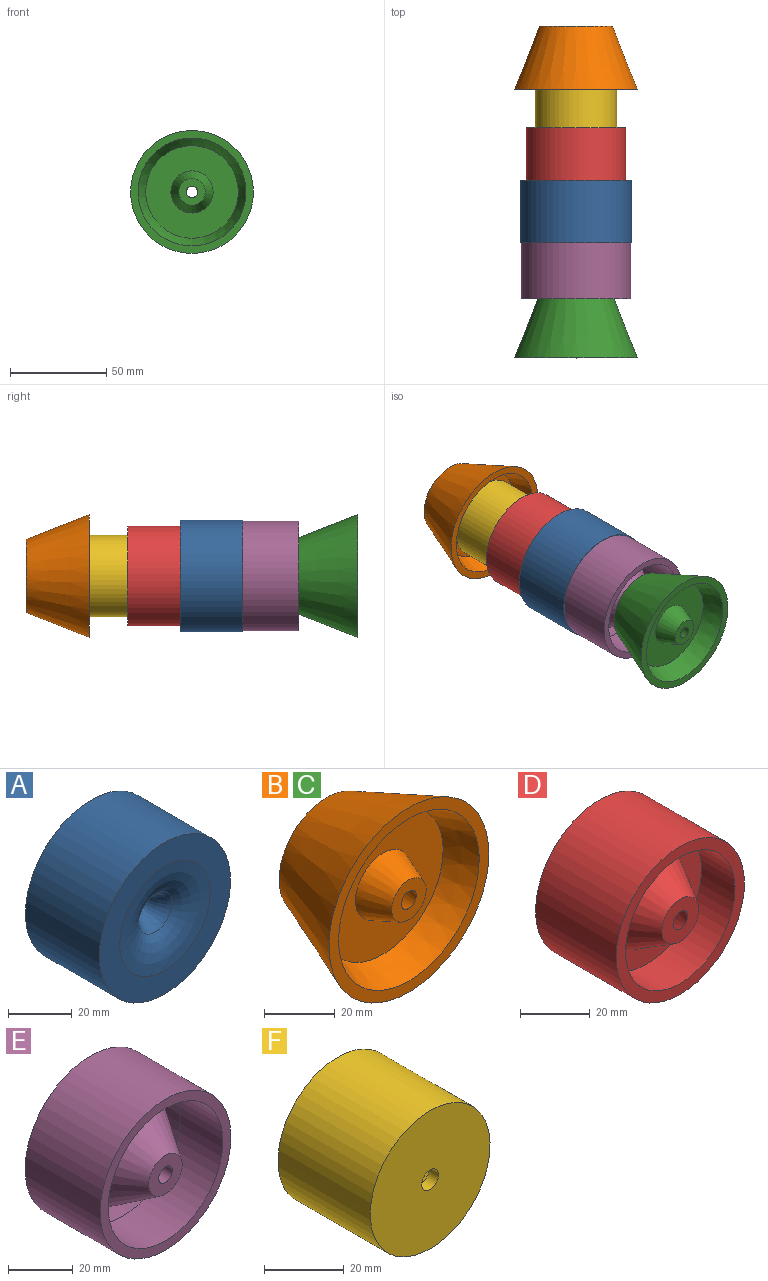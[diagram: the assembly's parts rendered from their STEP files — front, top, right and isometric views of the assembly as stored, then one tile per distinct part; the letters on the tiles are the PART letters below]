
ASSEMBLY  parts=6 mates=5
PART A: 14 faces, bbox 58.2x32.7x58.2 mm
  f0: revolved ~14.74x14.74mm, area 368.1mm2, adj f1,f6
  f1: revolved ~14.4x14.4mm, area 348.3mm2, adj f0,f2
  f2: revolved ~38.13x38.13mm, area 1043mm2, adj f1,f3
  f3: plane 58.18x58.18mm, normal (0,1,0), area 1516.7mm2, adj f2,f4
  f4: cylinder r=29.09mm len=58.18mm, axis (0,-1,0), area 5980.6mm2, adj f3,f5
  f5: plane 58.18x58.18mm, normal (0,-1,0), area 1398.9mm2, adj f4,f6
  f6: revolved ~40.05x40.05mm, area 1153.7mm2, adj f0,f5
  f7: revolved ~20.42x20.42mm, area 522.9mm2, adj f8,f13
  f8: revolved ~20.85x20.85mm, area 544.5mm2, adj f7,f9
  f9: revolved ~41.31x41.31mm, area 1061.5mm2, adj f8,f10
  f10: plane 50.57x50.57mm, normal (0,1,0), area 668.7mm2, adj f9,f11
  f11: cylinder r=25.29mm len=50.57mm, axis (0,-1,0), area 4153.1mm2, adj f10,f12
  f12: plane 50.57x50.57mm, normal (0,-1,0), area 782.4mm2, adj f11,f13
  f13: revolved ~39.52x39.52mm, area 960mm2, adj f7,f12
PART B: 13 faces, bbox 64x32.9x64 mm
  f0: cone r=6.91mm half-angle=21.4deg, axis (0,1,0), area 628.3mm2, adj f1,f7
  f1: plane 13.82x13.82mm, normal (0,-1,0), area 122.3mm2, adj f0,f2
  f2: cone r=15.84mm half-angle=21.4deg, axis (0,1,0), area 2085.6mm2, adj f1,f3
  f3: plane 38.08x38.08mm, normal (0,1,0), area 350.8mm2, adj f2,f4
  f4: cone r=31.98mm half-angle=21.5deg, axis (0,-1,0), area 5659.5mm2, adj f3,f5
  f5: plane 63.95x63.95mm, normal (0,-1,0), area 727.4mm2, adj f4,f6
  f6: cone r=24.1mm half-angle=21.1deg, axis (0,-1,0), area 1830.4mm2, adj f5,f7
  f7: plane 48.2x48.2mm, normal (0,-1,0), area 1445.3mm2, adj f0,f6
  f8: cone r=12.17mm half-angle=20.6deg, axis (0,1,0), area 957.8mm2, adj f9,f12
  f9: plane 45.5x45.5mm, normal (0,1,0), area 1161.2mm2, adj f8,f10
  f10: cone r=18.91mm half-angle=20.8deg, axis (0,-1,0), area 1419.4mm2, adj f9,f11
  f11: revolved ~37.81x37.81mm, area 562.2mm2, adj f10,f12
  f12: revolved ~34.99x34.99mm, area 522.6mm2, adj f8,f11
PART C: same geometry as B
PART D: 18 faces, bbox 52x32.7x52 mm
  f0: cylinder r=22.22mm len=44.44mm, axis (0,-1,0), area 1899.8mm2, adj f1,f10
  f1: plane 44.44x44.44mm, normal (0,-1,0), area 807.3mm2, adj f0,f2
  f2: cone r=7.47mm half-angle=30.2deg, axis (0,1,0), area 1130.7mm2, adj f1,f3
  f3: plane 14.94x14.94mm, normal (0,-1,0), area 147.5mm2, adj f2,f4
  f4: cone r=11.86mm half-angle=31.2deg, axis (0,1,0), area 800.5mm2, adj f3,f5
  f5: revolved ~23.72x23.72mm, area 561.3mm2, adj f4,f6
  f6: revolved ~16.31x16.31mm, area 302.4mm2, adj f5,f7
  f7: revolved ~34.1x34.1mm, area 732.9mm2, adj f6,f8
  f8: plane 52.05x52.05mm, normal (0,1,0), area 1214.3mm2, adj f7,f9
  f9: cylinder r=26.02mm len=52.05mm, axis (0,-1,0), area 5350.4mm2, adj f8,f10
  f10: plane 52.05x52.05mm, normal (0,-1,0), area 576.4mm2, adj f0,f9
  f11: plane 44.44x44.44mm, normal (0,1,0), area 643.3mm2, adj f12,f17
  f12: cylinder r=22.22mm len=44.44mm, axis (0,-1,0), area 1746.9mm2, adj f11,f13
  f13: plane 44.44x44.44mm, normal (0,-1,0), area 614mm2, adj f12,f14
  f14: revolved ~34.55x34.55mm, area 568.6mm2, adj f13,f15
  f15: revolved ~22.26x22.26mm, area 323.3mm2, adj f14,f16
  f16: revolved ~22.19x22.19mm, area 328.3mm2, adj f15,f17
  f17: revolved ~34x34mm, area 546.9mm2, adj f11,f16
PART E: 15 faces, bbox 57.1x32.7x57.1 mm
  f0: plane 14.62x14.62mm, normal (0,-1,0), area 140.2mm2, adj f1,f14
  f1: cylinder r=2.97mm len=32.72mm, axis (0,-1,0), area 611mm2, adj f0,f2
  f2: plane 13.06x13.06mm, normal (0,1,0), area 106.3mm2, adj f1,f3
  f3: cylinder r=6.53mm len=18.78mm, axis (0,-1,0), area 770.6mm2, adj f2,f4
  f4: revolved ~13.08x13.08mm, area 191.7mm2, adj f3,f5
  f5: revolved ~12.83x12.83mm, area 154.3mm2, adj f4,f6
  f6: plane 12.79x12.79mm, normal (0,1,0), area 7.1mm2, adj f5,f7
  f7: cone r=24.23mm half-angle=33.1deg, axis (0,1,0), area 3142.1mm2, adj f6,f8
  f8: plane 57.06x57.06mm, normal (0,1,0), area 712.3mm2, adj f7,f9
  f9: cylinder r=28.53mm len=57.06mm, axis (0,-1,0), area 5865.7mm2, adj f8,f10
  f10: plane 57.06x57.06mm, normal (0,-1,0), area 591.5mm2, adj f9,f11
  f11: cylinder r=25.01mm len=50.03mm, axis (0,-1,0), area 2923.2mm2, adj f10,f12
  f12: revolved ~50.75x50.75mm, area 1400.8mm2, adj f11,f13
  f13: plane 50.75x50.75mm, normal (0,-1,0), area 28.4mm2, adj f12,f14
  f14: cone r=7.31mm half-angle=33.1deg, axis (0,1,0), area 3346.1mm2, adj f0,f13
PART F: 12 faces, bbox 42.4x32.7x42.4 mm
  f0: plane 42.42x42.42mm, normal (0,-1,0), area 1385.8mm2, adj f1,f11
  f1: cylinder r=2.97mm len=5.94mm, axis (0,-1,0), area 63.5mm2, adj f0,f2
  f2: plane 34.82x34.82mm, normal (0,1,0), area 924.4mm2, adj f1,f3
  f3: cylinder r=17.41mm len=34.82mm, axis (0,-1,0), area 1316.8mm2, adj f2,f4
  f4: plane 34.82x34.82mm, normal (0,-1,0), area 905.7mm2, adj f3,f5
  f5: cylinder r=3.85mm len=7.69mm, axis (0,-1,0), area 81.2mm2, adj f4,f6
  f6: plane 34.82x34.82mm, normal (0,1,0), area 905.7mm2, adj f5,f7
  f7: cylinder r=17.41mm len=34.82mm, axis (0,-1,0), area 1153.1mm2, adj f6,f8
  f8: plane 34.82x34.82mm, normal (0,-1,0), area 924.4mm2, adj f7,f9
  f9: cylinder r=2.97mm len=5.94mm, axis (0,-1,0), area 63.1mm2, adj f8,f10
  f10: plane 42.42x42.42mm, normal (0,1,0), area 1385.8mm2, adj f9,f11
  f11: cylinder r=21.21mm len=42.42mm, axis (0,-1,0), area 4361mm2, adj f0,f10
PLACE A t=(-37.33,34.88,-55.19)mm
PLACE B t=(-35.71,114.98,-55.19)mm
PLACE C t=(-35.71,-24.99,-55.19)mm fixed
PLACE D t=(-34.26,62.2,-55.19)mm
PLACE E t=(-36.77,5.79,-55.19)mm
PLACE F t=(-29.45,89.28,-55.19)mm
MATE slider B.f0 <-> F.f1  axis (0,-1,0) through (-3.74,114.98,-55.19)mm
MATE slider A.f4 <-> C.f0  axis (0,-1,0) through (-3.74,58.31,-55.19)mm
MATE slider E.f1 <-> C.f0  axis (0,1,0) through (-3.74,38.51,-55.19)mm
MATE slider D.f0 <-> A.f4  axis (0,-1,0) through (-3.74,92.61,-55.19)mm
MATE slider F.f1 <-> A.f4  axis (0,1,0) through (-3.74,122,-55.19)mm
